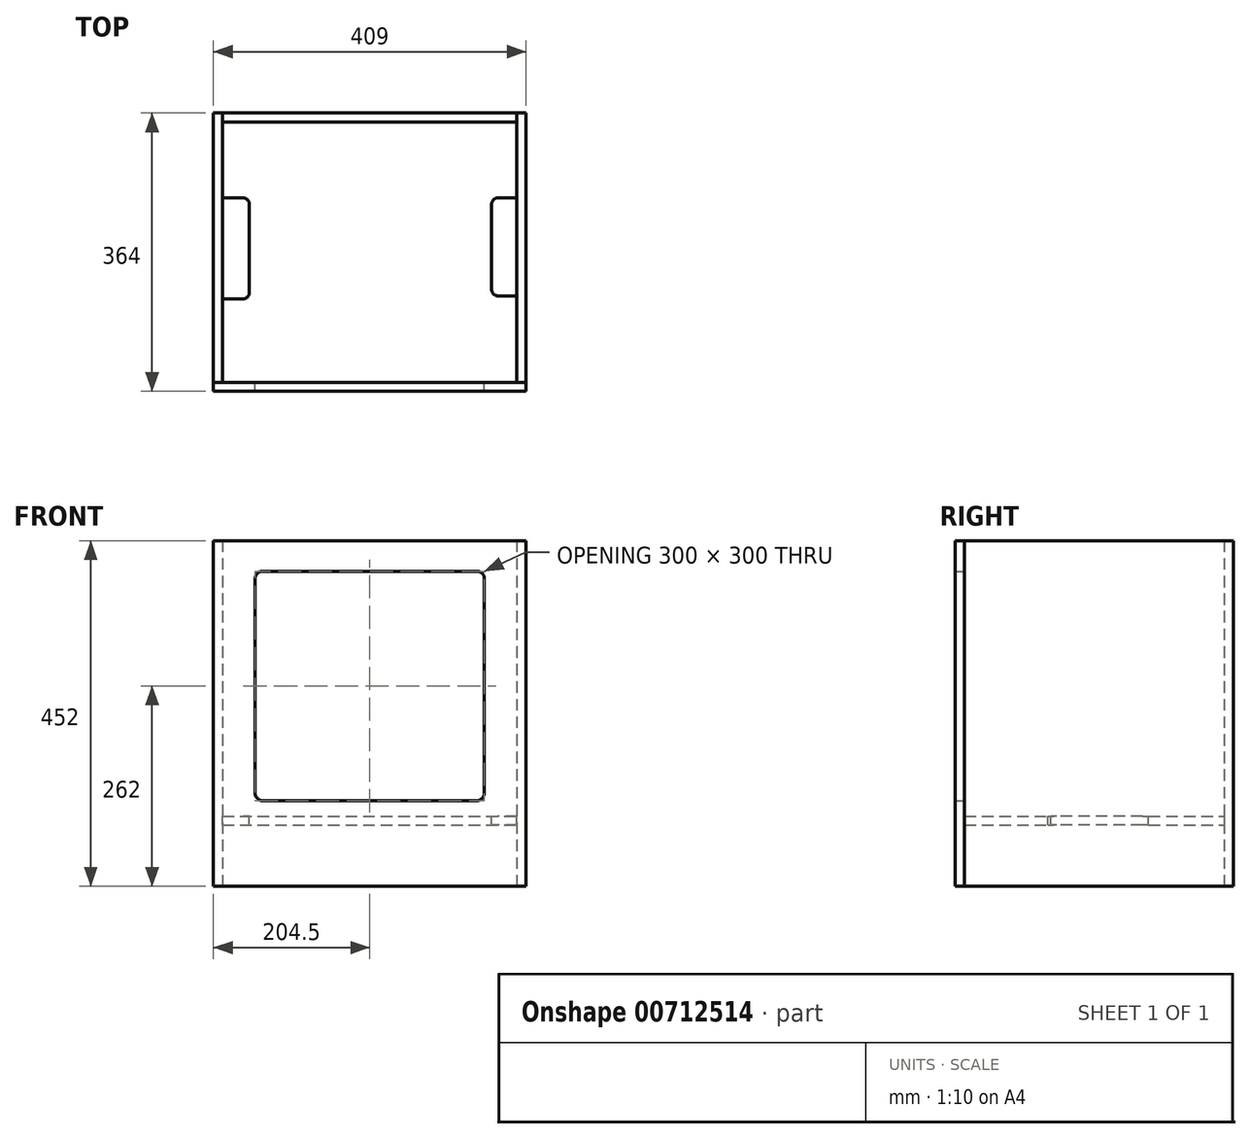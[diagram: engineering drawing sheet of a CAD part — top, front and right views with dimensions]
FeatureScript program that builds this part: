
annotation { "Feature Type Name" : "Feature", "Feature Type Description" : "" }
export const myFeature = defineFeature(function(context is Context, id is Id, definition is map)
    precondition{}
    {
        {
            var Q0;
            Q0=qCreatedBy(makeId("Front.planeOp"),FACE);
            var sketch = newSketch(context, id + "F0", { "sketchPlane" : qUnion([Q0])});
            skLineSegment(sketch, "E0.bottom", {"start": v(204.5, -226) * mm, "end": v(-204.5, -226) * mm});
            skLineSegment(sketch, "E0.top", {"start": v(204.5, 226) * mm, "end": v(-204.5, 226) * mm});
            skLineSegment(sketch, "E0.left", {"start": v(204.5, -226) * mm, "end": v(204.5, 226) * mm});
            skLineSegment(sketch, "E0.right", {"start": v(-204.5, -226) * mm, "end": v(-204.5, 226) * mm});
            skPoint(sketch, "E0.middle", {"position": v(0, 0) * mm});
            skLineSegment(sketch, "E1.bottom", {"start": v(140, -114) * mm, "end": v(-140, -114) * mm});
            skLineSegment(sketch, "E1.top", {"start": v(140, 186) * mm, "end": v(-140, 186) * mm});
            skLineSegment(sketch, "E1.left", {"start": v(150, -104) * mm, "end": v(150, 176) * mm});
            skLineSegment(sketch, "E1.right", {"start": v(-150, -104) * mm, "end": v(-150, 176) * mm});
            skPoint(sketch, "E1.middle", {"position": v(0, 36) * mm});
            skPoint(sketch, "E2.visualSharp", {"position": v(-150, 186) * mm});
            skArc(sketch, "E2.filletArc", {"start": v(-140, 186) * mm, "mid": v(-147.07, 183.07) * mm, "end": v(-150, 176) * mm});
            skPoint(sketch, "E3.visualSharp", {"position": v(150, 186) * mm});
            skArc(sketch, "E3.filletArc", {"start": v(150, 176) * mm, "mid": v(147.07, 183.07) * mm, "end": v(140, 186) * mm});
            skPoint(sketch, "E4.visualSharp", {"position": v(150, -114) * mm});
            skArc(sketch, "E4.filletArc", {"start": v(140, -114) * mm, "mid": v(147.07, -111.07) * mm, "end": v(150, -104) * mm});
            skPoint(sketch, "E5.visualSharp", {"position": v(-150, -114) * mm});
            skArc(sketch, "E5.filletArc", {"start": v(-150, -104) * mm, "mid": v(-147.07, -111.07) * mm, "end": v(-140, -114) * mm});
            skSolve(sketch);
        }
        {
            var Q0;
            Q0=makeQuery(id+"F0.imprint","IMPRINT",FACE,{"disambiguationData":[TD([[makeQuery(id+"F0.imprint","IMPRINT",EDGE,{"derivedFrom":sQuery(id+"F0.wireOp",EDGE,"E0.bottom")}),-1.0]])]});
            extrude(context, id + "F1", {"entities" : qUnion([Q0]), "depth" : 12 * mm, "offsetDistance" : 25 * mm});
        }
        {
            var Q0;
            Q0=makeQuery(id+"F1.opExtrude","CAP_FACE",FACE,{"disambiguationData":[OSD([sQuery(id+"F0.wireOp",EDGE,"E0.bottom"),sQuery(id+"F0.wireOp",EDGE,"E0.top"),sQuery(id+"F0.wireOp",EDGE,"E0.left"),sQuery(id+"F0.wireOp",EDGE,"E0.right"),sQuery(id+"F0.wireOp",EDGE,"E1.bottom"),sQuery(id+"F0.wireOp",EDGE,"E1.top"),sQuery(id+"F0.wireOp",EDGE,"E1.left"),sQuery(id+"F0.wireOp",EDGE,"E1.right"),sQuery(id+"F0.wireOp",EDGE,"E2.filletArc"),sQuery(id+"F0.wireOp",EDGE,"E3.filletArc"),sQuery(id+"F0.wireOp",EDGE,"E4.filletArc"),sQuery(id+"F0.wireOp",EDGE,"E5.filletArc")])],"isStart":true});
            var sketch = newSketch(context, id + "F2", { "sketchPlane" : qUnion([Q0])});
            skLineSegment(sketch, "E6.bottom", {"start": v(-204.5, 226) * mm, "end": v(-192.5, 226) * mm});
            skLineSegment(sketch, "E6.top", {"start": v(-204.5, -226) * mm, "end": v(-192.5, -226) * mm});
            skLineSegment(sketch, "E6.left", {"start": v(-204.5, 226) * mm, "end": v(-204.5, -226) * mm});
            skLineSegment(sketch, "E6.right", {"start": v(-192.5, 226) * mm, "end": v(-192.5, -226) * mm});
            skLineSegment(sketch, "E7.bottom", {"start": v(204.5, 226) * mm, "end": v(192.5, 226) * mm});
            skLineSegment(sketch, "E7.top", {"start": v(204.5, -226) * mm, "end": v(192.5, -226) * mm});
            skLineSegment(sketch, "E7.left", {"start": v(204.5, 226) * mm, "end": v(204.5, -226) * mm});
            skLineSegment(sketch, "E7.right", {"start": v(192.5, 226) * mm, "end": v(192.5, -226) * mm});
            skSolve(sketch);
        }
        {
            var Q0;
            Q0=makeQuery(id+"F2.imprint","IMPRINT",FACE,{"disambiguationData":[TD([[makeQuery(id+"F2.imprint","IMPRINT",EDGE,{"derivedFrom":sQuery(id+"F2.wireOp",EDGE,"E6.bottom")}),-1.0]])]});
            var Q1;
            Q1=makeQuery(id+"F2.imprint","IMPRINT",FACE,{"disambiguationData":[TD([[makeQuery(id+"F2.imprint","IMPRINT",EDGE,{"derivedFrom":sQuery(id+"F2.wireOp",EDGE,"E7.bottom")}),-1.0]])]});
            extrude(context, id + "F3", {"entities" : qUnion([Q0, Q1]), "depth" : 352 * mm, "offsetDistance" : 25 * mm});
        }
        {
            var Q0;
            Q0=makeQuery(id+"F3.opExtrude","SWEPT_FACE",FACE,{"disambiguationData":[OSD([sQuery(id+"F2.wireOp",EDGE,"E6.right")])]});
            var sketch = newSketch(context, id + "F4", { "sketchPlane" : qUnion([Q0])});
            skLineSegment(sketch, "E8.bottom", {"start": v(-352, 226) * mm, "end": v(-340, 226) * mm});
            skLineSegment(sketch, "E8.top", {"start": v(-352, -226) * mm, "end": v(-340, -226) * mm});
            skLineSegment(sketch, "E8.left", {"start": v(-352, 226) * mm, "end": v(-352, -226) * mm});
            skLineSegment(sketch, "E8.right", {"start": v(-340, 226) * mm, "end": v(-340, -226) * mm});
            skSolve(sketch);
        }
        {
            var Q0;
            Q0=makeQuery(id+"F4.imprint","IMPRINT",FACE,{"disambiguationData":[TD([[makeQuery(id+"F4.imprint","IMPRINT",EDGE,{"derivedFrom":sQuery(id+"F4.wireOp",EDGE,"E8.bottom")}),-1.0]])]});
            extrude(context, id + "F5", {"entities" : qUnion([Q0]), "endBound" : BoundingType.UP_TO_NEXT, "depth" : 25 * mm, "offsetDistance" : 25 * mm});
        }
        {
            var Q0;
            Q0=makeQuery(id+"F5.opExtrude","SWEPT_FACE",FACE,{"disambiguationData":[OSD([sQuery(id+"F4.wireOp",EDGE,"E8.right")])]});
            var sketch = newSketch(context, id + "F6", { "sketchPlane" : qUnion([Q0])});
            skLineSegment(sketch, "E9.bottom", {"start": v(-192.5, -146) * mm, "end": v(192.5, -146) * mm});
            skLineSegment(sketch, "E9.top", {"start": v(-192.5, -134) * mm, "end": v(192.5, -134) * mm});
            skLineSegment(sketch, "E9.left", {"start": v(-192.5, -146) * mm, "end": v(-192.5, -134) * mm});
            skLineSegment(sketch, "E9.right", {"start": v(192.5, -146) * mm, "end": v(192.5, -134) * mm});
            skSolve(sketch);
        }
        {
            var Q0;
            Q0=makeQuery(id+"F6.imprint","IMPRINT",FACE,{"disambiguationData":[TD([[makeQuery(id+"F6.imprint","IMPRINT",EDGE,{"derivedFrom":sQuery(id+"F6.wireOp",EDGE,"E9.bottom")}),1.0]])]});
            extrude(context, id + "F7", {"entities" : qUnion([Q0]), "endBound" : BoundingType.UP_TO_NEXT, "depth" : 25 * mm, "offsetDistance" : 25 * mm});
        }
        {
            var Q0;
            Q0=makeQuery(id+"F7.opExtrude","SWEPT_FACE",FACE,{"disambiguationData":[OSD([sQuery(id+"F6.wireOp",EDGE,"E9.top")])]});
            var sketch = newSketch(context, id + "F8", { "sketchPlane" : qUnion([Q0])});
            skLineSegment(sketch, "E10.bottom", {"start": v(-192.5, 241) * mm, "end": v(-165.5, 241) * mm});
            skLineSegment(sketch, "E10.top", {"start": v(-192.5, 109) * mm, "end": v(-165.5, 109) * mm});
            skLineSegment(sketch, "E10.left", {"start": v(-192.5, 241) * mm, "end": v(-192.5, 109) * mm});
            skLineSegment(sketch, "E10.right", {"start": v(-157.5, 233) * mm, "end": v(-157.5, 117) * mm});
            skLineSegment(sketch, "E11.bottom", {"start": v(192.5, 241) * mm, "end": v(167.5, 241) * mm});
            skLineSegment(sketch, "E11.top", {"start": v(192.5, 113) * mm, "end": v(167.5, 113) * mm});
            skLineSegment(sketch, "E11.left", {"start": v(192.5, 241) * mm, "end": v(192.5, 113) * mm});
            skLineSegment(sketch, "E11.right", {"start": v(159.5, 233) * mm, "end": v(159.5, 121) * mm});
            skPoint(sketch, "E12.visualSharp", {"position": v(-157.5, 241) * mm});
            skArc(sketch, "E12.filletArc", {"start": v(-157.5, 233) * mm, "mid": v(-159.84, 238.66) * mm, "end": v(-165.5, 241) * mm});
            skPoint(sketch, "E13.visualSharp", {"position": v(-157.5, 109) * mm});
            skArc(sketch, "E13.filletArc", {"start": v(-165.5, 109) * mm, "mid": v(-159.84, 111.34) * mm, "end": v(-157.5, 117) * mm});
            skPoint(sketch, "E14.visualSharp", {"position": v(159.5, 241) * mm});
            skArc(sketch, "E14.filletArc", {"start": v(167.5, 241) * mm, "mid": v(161.84, 238.66) * mm, "end": v(159.5, 233) * mm});
            skPoint(sketch, "E15.visualSharp", {"position": v(159.5, 113) * mm});
            skArc(sketch, "E15.filletArc", {"start": v(159.5, 121) * mm, "mid": v(161.84, 115.34) * mm, "end": v(167.5, 113) * mm});
            skSolve(sketch);
        }
        {
            var Q0;
            Q0=makeQuery(id+"F8.imprint","IMPRINT",FACE,{"disambiguationData":[TD([[makeQuery(id+"F8.imprint","IMPRINT",EDGE,{"derivedFrom":sQuery(id+"F8.wireOp",EDGE,"E10.bottom")}),-1.0]])]});
            var Q1;
            Q1=makeQuery(id+"F8.imprint","IMPRINT",FACE,{"disambiguationData":[TD([[makeQuery(id+"F8.imprint","IMPRINT",EDGE,{"derivedFrom":sQuery(id+"F8.wireOp",EDGE,"E11.bottom")}),1.0]])]});
            extrude(context, id + "F9", {"entities" : qUnion([Q0, Q1]), "operationType" : NewBodyOperationType.REMOVE, "endBound" : BoundingType.THROUGH_ALL, "oppositeDirection" : true, "depth" : 25 * mm, "offsetDistance" : 25 * mm});
        }
    });
